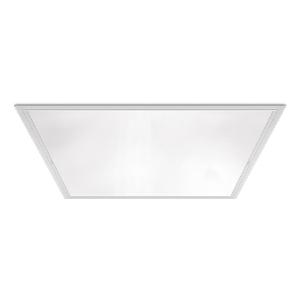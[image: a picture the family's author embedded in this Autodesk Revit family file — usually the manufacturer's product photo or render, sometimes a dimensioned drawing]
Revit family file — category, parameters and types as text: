
# Revit family: 3f_filippi_-_l_340_luce_diffusa_lgs_3f_filippi_-_23864_-_l_340_38w-840_dali_lgs_596x596
name_source: partatom
category: Lighting Fixtures
units: mm (PartAtom-declared; Revit-internal decimal feet)

## family parameters
Cut with Voids When Loaded = No
Host = Face
Light Source = No
Part Type = Normal
Room Calculation Point = No
Round Connector Dimension = Use Diameter
Shared = No

## types (1)
- 3F Filippi - L 340 Luce Diffusa LGS (1 x LED, 5677 lm, 43 W, 4000 K)
    Apparent Load = 43 VA
    Approval mark = ENEC
    CIE Flux Codes = 67 92 98 100 100
    Color Rendering = 80
    Color Temperature = 4000 K
    Control Gear = Electronic transformer
    Default Elevation = 1800 mm
    Description = ILLUMINOTECHNICAL
Luminous efficiency 100% (DLOR 100%, ULOR 0%).
Initial luminous flux of the luminaire 5677 lm.
Direct symmetric distribution.
Installation Interdistance Transv.D = 1.19 x hu - Long.D = 1.17 x hu.
Average luminance <3000 cd/m² for radial angles >65°.
Tabular UGR (CIE 117 - 4H-8H; S=0.25H; 70/50/20): RUG 17.8 - 17.8.
Beam angle: 87° - 86°.
Luminous efficacy 132 lm/W.
Lifetime (L93/B10): 30000 h. (tq+25°C)
Lifetime (L90/B10): 50000 h. (tq+25°C)
Lifetime (L85/B10): 80000 h. (tq+25°C)
Lifetime (L80/B10): 100000 h. (tq+25°C)
Sudden decreased luminous flux after 50000 hours: 0% (C0).
Photobiological safety in compliance with IEC/TR 62778: RG0 risk exempt, (IEC 62471).
In compliance with IEC/EN 62722-2-1 - IEC/EN 62717 standards.

SOURCE
Squared LED module 38W/840.
Energy efficiency class (UE 2019/2020 - UE 2019/2015): C.
CIE 13.3 Colour rendering index: CRI >80 (R9 <50%).
IES TM-30 Fidelity Index: Rf = 84 Rg = 95.
CCT nominal colour temperature 4000 K.
Colour initial tolerance (MacAdam): SDCM 3.

MECHANICAL
Housing in hot-galvanised steel, painted in white polyester.
Perimetral frame in white polycarbonate.
LGS micro-prismatic flat diffuser in transparent methacrylate (PMMA), multi-lenticular exterior, anti-glare.
Anti-glare opal polycarbonate filter for brightness uniformity.
Luminaire with limited surface temperature. - D - (EN 60598-2-24)
Dimensions: 596x596 mm, height 80 mm. Weight 4.4 kg.
IP40 protection degree.
Mechanical strength to impacts IK06 (1 joule).
Glow-wire test resistance 650°C.

ELECTRICAL
Wiring on a separate unit.
Halogen Free DALI-2 DATI (Parts 251, 252, 253), PUSH-DIM, electronic wiring 230V-50/60Hz, power factor 0.95 at full load, THD <25%, constant output current, SELV, class II, 1 driver, 1 DALI addresse.
Power of the luminaire 43 W.
CE - IEC 60598-1 - EN 60598-1.
SAFE FLICKER: PstLM=<1 and SVM=<0.4 (IEC TR 61547-1 and IEC TR 63158), to ensure a more comfortable and safe light.
Luminaire compliant with EN 60598-2-22 for power supply from a centralised emergency system CPSS (Central Power Supply System), not incorporated in the luminaire - high risk areas excluded. The default power and flux are 100% in AC and 15% in DC.
Ambient temperature from 0°C to +40°C.
Temperature class T6 max 85°C.
Relative humidity UR: <85%.

INSTALLATION
Lay-on or pull-up recessed fitting using frame accessory.
All accessories dedicated to this product are available on the Catalog and on our website www.3F-Filippi.com.

APPLICATIONS
Suitable product for food production plants (HACCP), IFS (Food Version 6), BRC (GSFS Food Version 7).
Environments: with VDTs, meeting rooms, offices.
Environments: architectural, commercial, staterooms, banks.
Environments where demanding visual tasks are performed and soft diffuse light is required for optimal visual comfort and total shielding of the light source.

LIGHT MANAGEMENT
Recommended minimum setting: 10%.
The luminaire, equipped with (DALI-2 DATI) driver, can be controlled manually with 3F Easy Dim technology or automatically/manually with wired or wireless DALI/D2D control systems.
The D2D driver guarantees interoperability with other devices with the same certification by making the following information available:
Device Data (Part 251), Energy Report (Part 252), Diagnosis & Maintenance (Part 253).
In electrical systems without a regulation system (manual or automatic) and DALI bus, a suitable jumper must be made on the DA-DA terminals of the appliance.

WARNING
Luminaire designed for disposal/recycling at end-of-life.
Replaceable (LED only) light source by a professional. Replaceable control gear by a professional.
    Height = 0 mm  [stored 0 ft]
    Lamp = 1 x LED
    Lamp Light Flux = 5677 lm
    Lamp Power = 43 W
    Lamp count = 1
    Length = 596 mm
    Lifetime = 50000 h
    Luminous efficacy = 132 lm/W
    Manufacturer = 3F Filippi
    ModVariant = No
    Model = 3F Filippi - 23864 - L 340 38W-840 DALI LGS 596x596
    Mounting Place = Ceiling
    Mounting Type = Recessed
    Number of Poles = 1
    OnlyDefault = Yes
    Power Factor = 1
    Product Name = 3F Filippi - L 340 Luce Diffusa LGS
    Product group = recessed luminaire
    ProductGroupID = 4
    Protection Class = Protection class II
    Protection Degree = IP 40
    RLX_Detail_Level = 1
    RLX_Emergency_Light_Flux = 0 lm
    RLX_Emergency_Type = 0
    RLX_Emergency_Type_DB = No
    RlxData = <blob elided: 155701 chars, md5=000b3dcc>
    Socket = socket
    Standby Power = 0 W
    System Light Flux = 5677 lm
    System Power = 43 W
    Type Comments = Product without accessories
    Type Image = 3ffilippi_l_340_luce_diffusa_lgs.jpg
    URL = http://relux.com
    VarID = ---
    Voltage = 0 V
    Weight = 0.00 kg
    Width = 596 mm

note: [stored X ft] marks values corroborated as IEEE doubles in the binary element streams (Revit-internal decimal feet)

## geometry (parser evidence)
native form markers: Blend x4, Sweep x10
no freeform markers — native parametric forms only
